# Revit family: HOB_GEN_Torquay_Standard
name_source: partatom
category: Generic Models
units: mm (PartAtom-declared; Revit-internal decimal feet)

## family parameters
Always vertical = Yes
Can host rebar = No
Cut with Voids When Loaded = No
Maintain Annotation Orientation = No
Part Type = Normal
Room Calculation Point = No
Round Connector Dimension = Use Diameter
Shared = Yes
Work Plane-Based = No

## types (1)
- Torquay_W392xH1860
    BattenDepth = 20 mm  [stored 0.0656168 ft]
    BattenSpacing = 28 mm  [stored 0.0918635 ft]
    BattenWidth = 20 mm  [stored 0.0656168 ft]
    Battens Material = Bamboo_horizontalGrain
    BattensBottomOffset = 0 mm  [stored 0 ft]
    BattensTopOffset = 0 mm  [stored 0 ft]
    Cost = 286 $
    Default Elevation = 0 mm  [stored 0 ft]
    Description = 20x30 mm slat / 392 mm standard width / 1800/2100/2400 mm Standard height
    Manufacturer = HOB
    Model = Torquay
    PanelCost = 300 $
    RailBottomOffset = 50 mm  [stored 0.164042 ft]
    RailTopOffset = 50 mm  [stored 0.164042 ft]
    SideOffset = 14 mm  [stored 0.0459318 ft]
    Support Rail Material = HOB_Black
    URL = https://houseofbamboo.com.au

note: [stored X ft] marks values corroborated as IEEE doubles in the binary element streams (Revit-internal decimal feet)

## geometry (parser evidence)
native form markers: Sweep x8
no freeform markers — native parametric forms only
